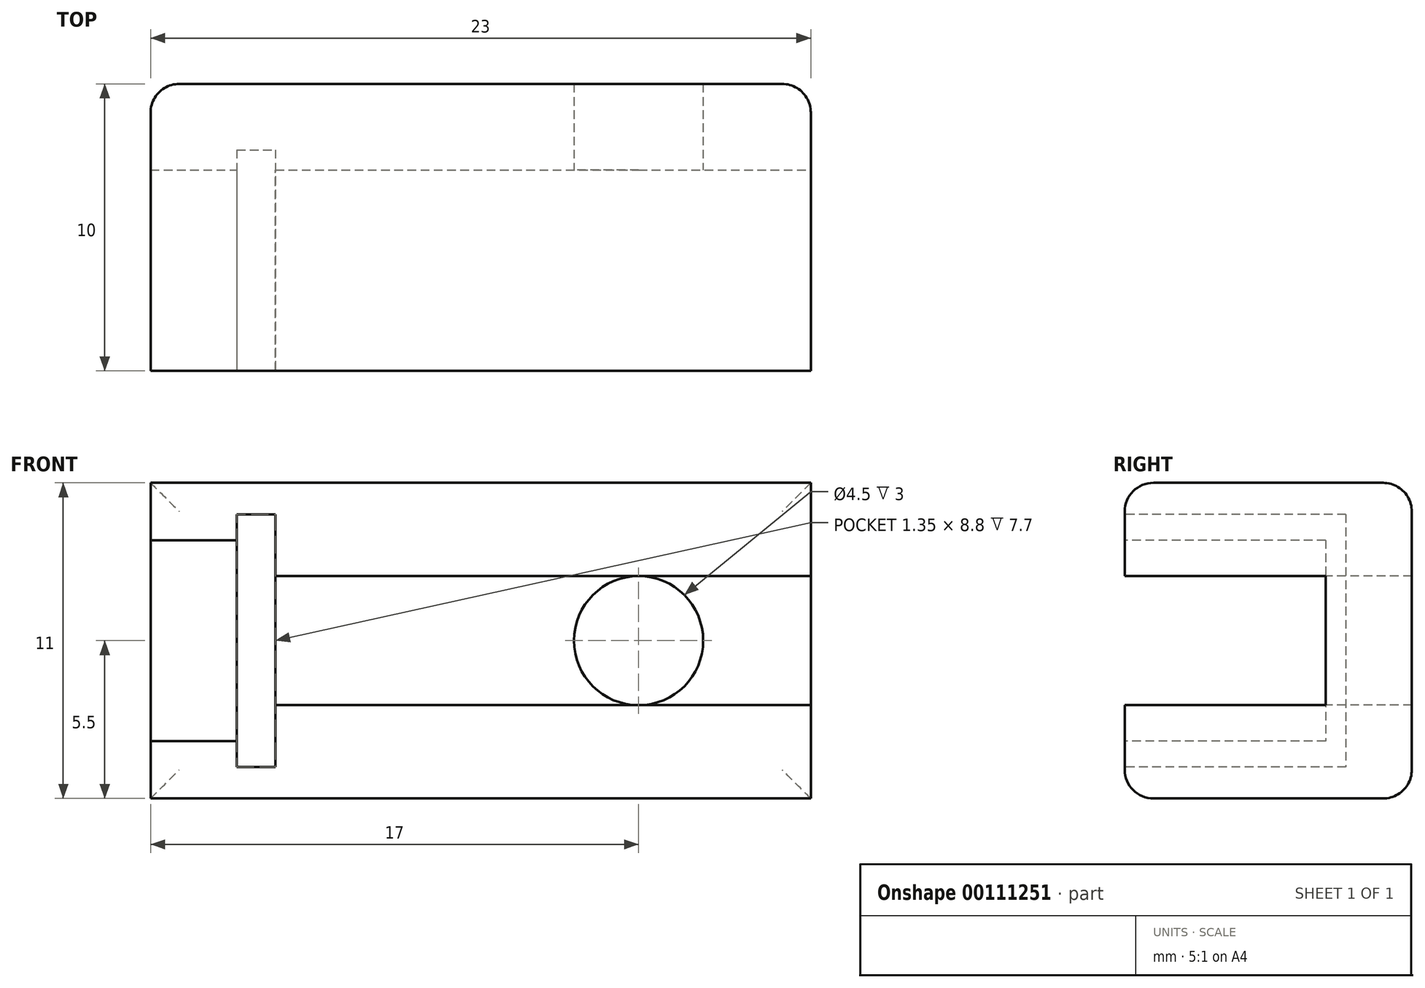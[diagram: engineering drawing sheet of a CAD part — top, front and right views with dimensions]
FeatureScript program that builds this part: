
annotation { "Feature Type Name" : "Feature", "Feature Type Description" : "" }
export const myFeature = defineFeature(function(context is Context, id is Id, definition is map)
    precondition{}
    {
        {
            var Q0;
            Q0=qCreatedBy(makeId("Front.planeOp"),FACE);
            var sketch = newSketch(context, id + "F0", { "sketchPlane" : qUnion([Q0])});
            skLineSegment(sketch, "E0.bottom", {"start": v(-7.5, 5.5) * mm, "end": v(7.5, 5.5) * mm});
            skLineSegment(sketch, "E0.top", {"start": v(-7.5, -5.5) * mm, "end": v(7.5, -5.5) * mm});
            skLineSegment(sketch, "E0.left", {"start": v(-7.5, 5.5) * mm, "end": v(-7.5, -5.5) * mm});
            skLineSegment(sketch, "E0.right", {"start": v(7.5, 5.5) * mm, "end": v(7.5, -5.5) * mm});
            skPoint(sketch, "E0.middle", {"position": v(0, 0) * mm});
            skSolve(sketch);
        }
        {
            var Q0;
            Q0 = qSketchRegion(id + "F0", true);
            extrude(context, id + "F1", {"entities" : qUnion([Q0]), "depth" : 10 * mm});
        }
        {
            var Q0;
            Q0=makeQuery(id+"F1.opExtrude","CAP_FACE",FACE,{"disambiguationData":[OSD([sQuery(id+"F0.wireOp",EDGE,"E0.bottom"),sQuery(id+"F0.wireOp",EDGE,"E0.top"),sQuery(id+"F0.wireOp",EDGE,"E0.left"),sQuery(id+"F0.wireOp",EDGE,"E0.right")])],"isStart":false});
            var sketch = newSketch(context, id + "F2", { "sketchPlane" : qUnion([Q0])});
            skLineSegment(sketch, "E1.bottom", {"start": v(-7.5, 2.25) * mm, "end": v(7.5, 2.25) * mm});
            skLineSegment(sketch, "E1.top", {"start": v(-7.5, -2.25) * mm, "end": v(7.5, -2.25) * mm});
            skLineSegment(sketch, "E1.left", {"start": v(-7.5, 2.25) * mm, "end": v(-7.5, -2.25) * mm});
            skLineSegment(sketch, "E1.right", {"start": v(7.5, 2.25) * mm, "end": v(7.5, -2.25) * mm});
            skPoint(sketch, "E1.middle", {"position": v(0, 0) * mm});
            skSolve(sketch);
        }
        {
            var Q0;
            Q0=makeQuery(id+"F2.imprint","IMPRINT",FACE,{"disambiguationData":[TD([[makeQuery(id+"F2.imprint","IMPRINT",EDGE,{"derivedFrom":sQuery(id+"F2.wireOp",EDGE,"E1.bottom")}),-1.0]])]});
            extrude(context, id + "F3", {"entities" : qUnion([Q0]), "operationType" : NewBodyOperationType.REMOVE, "oppositeDirection" : true, "depth" : 7 * mm});
        }
        {
            var Q0;
            {var subQ0=sQuery(id+"F0.wireOp",EDGE,"E0.bottom");var subQ1=sQuery(id+"F0.wireOp",EDGE,"E0.left");var subQ2=sQuery(id+"F0.wireOp",EDGE,"E0.right");Q0=makeQuery(id+"F3.boolean.opBoolean","SPLIT",FACE,{"disambiguationData":[TD([makeQuery(id+"F1.opExtrude","SWEPT_FACE",FACE,{"disambiguationData":[OSD([subQ0])]})])],"derivedFrom":makeQuery(id+"F1.opExtrude","CAP_FACE",FACE,{"disambiguationData":[OSD([subQ0,sQuery(id+"F0.wireOp",EDGE,"E0.top"),subQ1,subQ2])],"isStart":false})});}
            var sketch = newSketch(context, id + "F4", { "sketchPlane" : qUnion([Q0])});
            skLineSegment(sketch, "E2.bottom", {"start": v(-7.5, 3.5) * mm, "end": v(-4.5, 3.5) * mm});
            skLineSegment(sketch, "E2.top", {"start": v(-7.5, -3.5) * mm, "end": v(-4.5, -3.5) * mm});
            skLineSegment(sketch, "E2.left", {"start": v(-7.5, 3.5) * mm, "end": v(-7.5, -3.5) * mm});
            skLineSegment(sketch, "E2.right", {"start": v(-4.5, 3.5) * mm, "end": v(-4.5, -3.5) * mm});
            skSolve(sketch);
        }
        {
            var Q0;
            Q0 = qSketchRegion(id + "F4", true);
            extrude(context, id + "F5", {"entities" : qUnion([Q0]), "operationType" : NewBodyOperationType.REMOVE, "oppositeDirection" : true, "depth" : 7 * mm});
        }
        {
            var Q0;
            {var subQ0=sQuery(id+"F0.wireOp",EDGE,"E0.bottom");var subQ1=sQuery(id+"F0.wireOp",EDGE,"E0.left");var subQ2=sQuery(id+"F0.wireOp",EDGE,"E0.right");Q0=makeQuery(id+"F3.boolean.opBoolean","SPLIT",FACE,{"disambiguationData":[TD([makeQuery(id+"F1.opExtrude","SWEPT_FACE",FACE,{"disambiguationData":[OSD([subQ0])]})])],"derivedFrom":makeQuery(id+"F1.opExtrude","CAP_FACE",FACE,{"disambiguationData":[OSD([subQ0,sQuery(id+"F0.wireOp",EDGE,"E0.top"),subQ1,subQ2])],"isStart":false})});}
            var sketch = newSketch(context, id + "F6", { "sketchPlane" : qUnion([Q0])});
            skLineSegment(sketch, "E3.bottom", {"start": v(-4.5, 4.4) * mm, "end": v(-3.15, 4.4) * mm});
            skLineSegment(sketch, "E3.top", {"start": v(-4.5, -4.4) * mm, "end": v(-3.15, -4.4) * mm});
            skLineSegment(sketch, "E3.left", {"start": v(-4.5, 4.4) * mm, "end": v(-4.5, -4.4) * mm});
            skLineSegment(sketch, "E3.right", {"start": v(-3.15, 4.4) * mm, "end": v(-3.15, -4.4) * mm});
            skSolve(sketch);
        }
        {
            var Q0;
            Q0 = qSketchRegion(id + "F6", true);
            extrude(context, id + "F7", {"entities" : qUnion([Q0]), "operationType" : NewBodyOperationType.REMOVE, "oppositeDirection" : true, "depth" : 7.7 * mm});
        }
        {
            var Q0;
            Q0=makeQuery(id+"F1.opExtrude","SWEPT_FACE",FACE,{"disambiguationData":[OSD([sQuery(id+"F0.wireOp",EDGE,"E0.right")])]});
            var sketch = newSketch(context, id + "F8", { "sketchPlane" : qUnion([Q0])});
            skLineSegment(sketch, "E4", {"start": v(-3, 2.25) * mm, "end": v(0, 2.25) * mm});
            skLineSegment(sketch, "E5", {"start": v(-3, -2.25) * mm, "end": v(0, -2.25) * mm});
            skSolve(sketch);
        }
        {
            var Q0;
            {var subQ5=sQuery(id+"F8.wireOp",EDGE,"E4");Q0=makeQuery(id+"F8.imprint","IMPRINT",FACE,{"disambiguationData":[TD([[makeQuery(id+"F8.imprint","IMPRINT",EDGE,{"derivedFrom":subQ5}),1.0]])]});}
            var Q1;
            {var subQ4=sQuery(id+"F8.wireOp",EDGE,"E5");Q1=makeQuery(id+"F8.imprint","IMPRINT",FACE,{"disambiguationData":[TD([[makeQuery(id+"F8.imprint","IMPRINT",EDGE,{"derivedFrom":subQ4}),-1.0]])]});}
            extrude(context, id + "F9", {"entities" : qUnion([Q0, Q1]), "operationType" : NewBodyOperationType.ADD, "depth" : 8 * mm});
        }
        {
            var Q0;
            Q0=makeQuery(id+"F1.opExtrude","SWEPT_FACE",FACE,{"disambiguationData":[OSD([sQuery(id+"F0.wireOp",EDGE,"E0.right")])]});
            extrude(context, id + "F10", {"entities" : qUnion([Q0]), "operationType" : NewBodyOperationType.ADD, "depth" : 8 * mm});
        }
        {
            var Q0;
            {var subQ0=sQuery(id+"F0.wireOp",EDGE,"E0.right");var subQ1=makeQuery(id+"F1.opExtrude","CAP_EDGE",EDGE,{"disambiguationData":[OSD([subQ0])],"isStart":true});var subQ2=sQuery(id+"F0.wireOp",EDGE,"E0.top");var subQ3=sQuery(id+"F0.wireOp",EDGE,"E0.bottom");Q0=makeQuery(id+"F10.boolean.opBoolean","MERGE",FACE,{"derivedFrom":[makeQuery(id+"F9.boolean.opBoolean","MERGE",FACE,{"derivedFrom":[makeQuery(id+"F1.opExtrude","CAP_FACE",FACE,{"disambiguationData":[OSD([subQ3,subQ2,sQuery(id+"F0.wireOp",EDGE,"E0.left"),subQ0])],"isStart":true}),makeQuery(id+"F9.opExtrude","SWEPT_FACE",FACE,{"disambiguationData":[OSD([subQ0]),TDD([makeQuery(id+"F8.imprint","IMPRINT",EDGE,{"disambiguationData":[TD([[makeQuery(id+"F8.imprint","INTERSECT",VERTEX,{"derivedFrom":[subQ1,sQuery(id+"F8.wireOp",EDGE,"E4")]}),1.0]])],"derivedFrom":subQ1})])]}),makeQuery(id+"F9.opExtrude","SWEPT_FACE",FACE,{"disambiguationData":[OSD([subQ0]),TDD([makeQuery(id+"F8.imprint","IMPRINT",EDGE,{"disambiguationData":[TD([[makeQuery(id+"F8.imprint","INTERSECT",VERTEX,{"derivedFrom":[subQ1,sQuery(id+"F8.wireOp",EDGE,"E5")]}),-1.0]])],"derivedFrom":subQ1})])]})]}),makeQuery(id+"F10.opExtrude","SWEPT_FACE",FACE,{"disambiguationData":[OSD([subQ0])]})]});}
            fillet(context, id + "F11", {"entities" : qUnion([Q0]), "radius" : 1 * mm, "tangentPropagation" : true, "allowEdgeOverflow" : false});
        }
        {
            var Q0;
            {var subQ0=sQuery(id+"F0.wireOp",EDGE,"E0.bottom");var subQ1=sQuery(id+"F0.wireOp",EDGE,"E0.right");Q0=makeQuery(id+"F9.boolean.opBoolean","MERGE",EDGE,{"derivedFrom":[makeQuery(id+"F1.opExtrude","CAP_EDGE",EDGE,{"disambiguationData":[OSD([subQ0])],"isStart":false}),makeQuery(id+"F9.opExtrude","SWEPT_EDGE",EDGE,{"disambiguationData":[OSD([subQ0,subQ1]),TDD([makeQuery(id+"F8.imprint","INTERSECT",VERTEX,{"derivedFrom":[makeQuery(id+"F1.opExtrude","SWEPT_EDGE",EDGE,{"disambiguationData":[OSD([subQ0,subQ1])]}),makeQuery(id+"F3.boolean.opBoolean","SPLIT",EDGE,{"disambiguationData":[TD([makeQuery(id+"F1.opExtrude","SWEPT_FACE",FACE,{"disambiguationData":[OSD([subQ0])]})])],"derivedFrom":makeQuery(id+"F1.opExtrude","CAP_EDGE",EDGE,{"disambiguationData":[OSD([subQ1])],"isStart":false})})]})])]})]});}
            var Q1;
            {var subQ0=sQuery(id+"F0.wireOp",EDGE,"E0.right");var subQ1=sQuery(id+"F0.wireOp",EDGE,"E0.top");Q1=makeQuery(id+"F9.boolean.opBoolean","MERGE",EDGE,{"derivedFrom":[makeQuery(id+"F1.opExtrude","CAP_EDGE",EDGE,{"disambiguationData":[OSD([subQ1])],"isStart":false}),makeQuery(id+"F9.opExtrude","SWEPT_EDGE",EDGE,{"disambiguationData":[OSD([subQ1,subQ0]),TDD([makeQuery(id+"F8.imprint","INTERSECT",VERTEX,{"derivedFrom":[makeQuery(id+"F1.opExtrude","SWEPT_EDGE",EDGE,{"disambiguationData":[OSD([subQ1,subQ0])]}),makeQuery(id+"F3.boolean.opBoolean","SPLIT",EDGE,{"disambiguationData":[TD([makeQuery(id+"F1.opExtrude","SWEPT_FACE",FACE,{"disambiguationData":[OSD([subQ1])]})])],"derivedFrom":makeQuery(id+"F1.opExtrude","CAP_EDGE",EDGE,{"disambiguationData":[OSD([subQ0])],"isStart":false})})]})])]})]});}
            fillet(context, id + "F12", {"entities" : qUnion([Q0, Q1]), "radius" : 1 * mm, "tangentPropagation" : true, "allowEdgeOverflow" : false});
        }
        {
            var Q0;
            {var subQ0=sQuery(id+"F2.wireOp",EDGE,"E1.right");var subQ1=sQuery(id+"F2.wireOp",EDGE,"E1.bottom");var subQ2=sQuery(id+"F2.wireOp",EDGE,"E1.top");Q0=makeQuery(id+"F10.boolean.opBoolean","MERGE",FACE,{"derivedFrom":[makeQuery(id+"F7.boolean.opBoolean","SPLIT",FACE,{"disambiguationData":[TD([makeQuery(id+"F1.opExtrude","SWEPT_FACE",FACE,{"disambiguationData":[OSD([sQuery(id+"F0.wireOp",EDGE,"E0.right")])]})])],"derivedFrom":makeQuery(id+"F5.boolean.opBoolean","MERGE",FACE,{"derivedFrom":[makeQuery(id+"F3.boolean.opBoolean","COPY",FACE,{"derivedFrom":makeQuery(id+"F3.opExtrude","CAP_FACE",FACE,{"disambiguationData":[OSD([subQ1,subQ2,sQuery(id+"F2.wireOp",EDGE,"E1.left"),subQ0])],"isStart":false})}),makeQuery(id+"F5.opExtrude","CAP_FACE",FACE,{"disambiguationData":[OSD([sQuery(id+"F4.wireOp",EDGE,"E2.bottom"),sQuery(id+"F4.wireOp",EDGE,"E2.top"),sQuery(id+"F4.wireOp",EDGE,"E2.left"),sQuery(id+"F4.wireOp",EDGE,"E2.right")])],"isStart":false})]})}),makeQuery(id+"F10.opExtrude","SWEPT_FACE",FACE,{"disambiguationData":[OSD([subQ0])]})]});}
            var sketch = newSketch(context, id + "F13", { "sketchPlane" : qUnion([Q0])});
            skPoint(sketch, "E6", {"position": v(9.5, 0) * mm});
            skCircle(sketch, "E7", {"center": v(9.5, 0) * mm, "radius": 2.25 * mm});
            skSolve(sketch);
        }
        {
            var Q0;
            Q0 = qSketchRegion(id + "F13", true);
            extrude(context, id + "F14", {"entities" : qUnion([Q0]), "operationType" : NewBodyOperationType.REMOVE, "oppositeDirection" : true, "depth" : 25 * mm});
        }
    });
